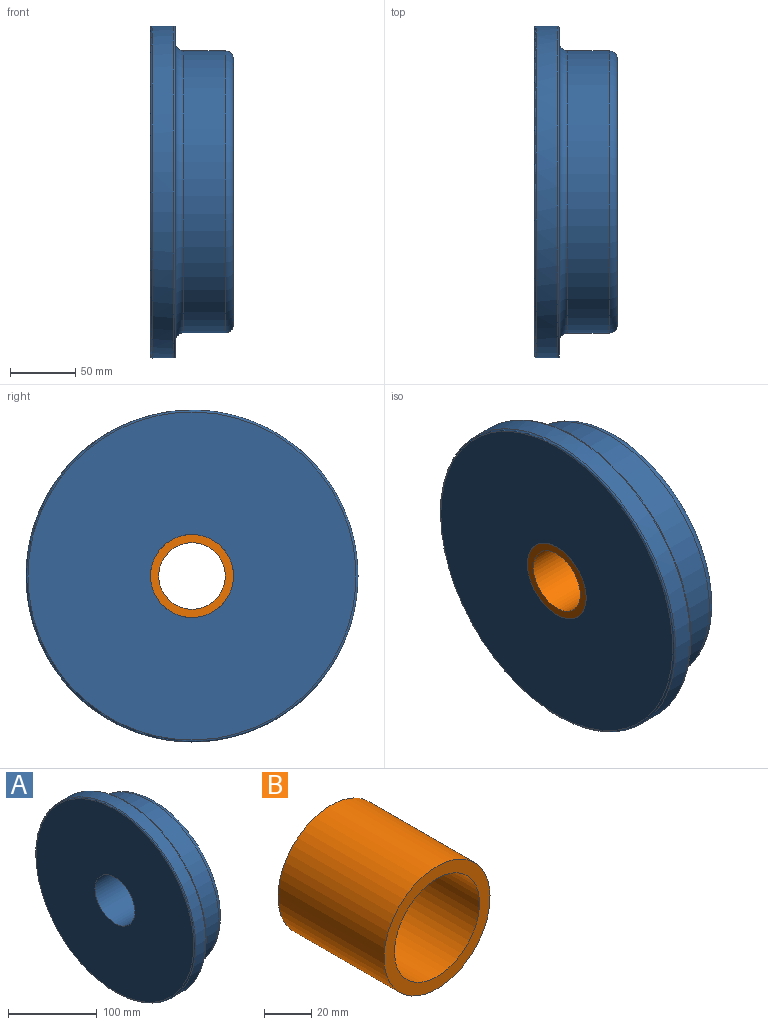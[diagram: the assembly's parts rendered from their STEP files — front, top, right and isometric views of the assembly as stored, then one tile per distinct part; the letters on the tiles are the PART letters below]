
ASSEMBLY  parts=2 mates=1
PART A: 10 faces, bbox 63.5x274.9x274.9 mm
  f0: plane 250.95x250.95mm, normal (-1,0,0), area 46295mm2, adj f6,f9
  f1: plane 203.2x203.2mm, normal (1,0,0), area 29262.4mm2, adj f3,f9
  f2: torus R=114.3mm, axis (-1,0,0), area 6910.1mm2, adj f4,f8
  f3: torus R=101.6mm, axis (-1,0,0), area 6620.8mm2, adj f1,f4
  f4: cylinder r=107.95mm len=215.9mm, axis (1,0,0), area 21535.1mm2, adj f2,f3
  f5: cylinder r=127mm len=254mm, axis (1,0,0), area 12769mm2, adj f6,f7
  f6: torus R=125.48mm, axis (1,0,0), area 1901.9mm2, adj f0,f5
  f7: torus R=125.48mm, axis (-1,0,0), area 1901.9mm2, adj f5,f8
  f8: plane 250.95x250.95mm, normal (1,0,0), area 8418.6mm2, adj f2,f7
  f9: cylinder r=31.75mm len=63.5mm, axis (1,0,0), area 12667.7mm2, adj f0,f1
PART B: 4 faces, bbox 63.5x63.5x63.5 mm
  f0: cylinder r=25.43mm len=63.5mm, axis (0,1,0), area 10144.3mm2, adj f2,f3
  f1: cylinder r=31.75mm len=63.5mm, axis (0,1,0), area 12667.7mm2, adj f2,f3
  f2: plane 63.5x63.5mm, normal (0,-1,0), area 1136mm2, adj f0,f1
  f3: plane 63.5x63.5mm, normal (0,1,0), area 1136mm2, adj f0,f1
PLACE A t=(-63.5,0,0)mm
PLACE B rot(axis=(-0.58,0.58,0.58),120deg) t=(-63.5,0,0)mm
MATE fastened B.f0 <-> A.f2  axis (1,0,0) through (0,0,0)mm
